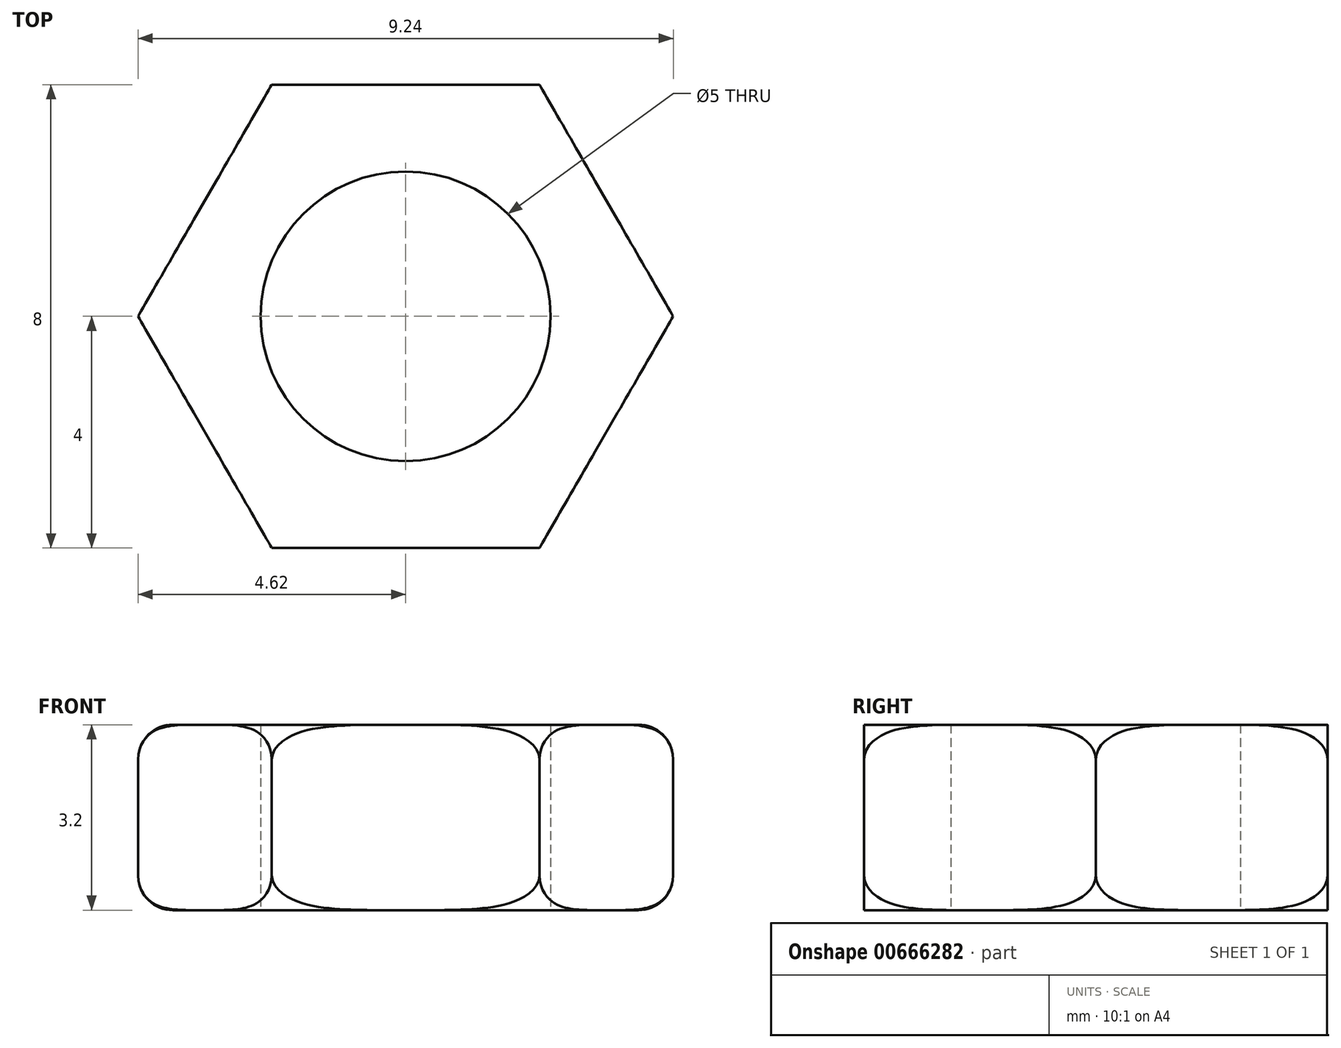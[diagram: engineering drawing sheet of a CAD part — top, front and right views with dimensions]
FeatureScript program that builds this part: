
annotation { "Feature Type Name" : "Feature", "Feature Type Description" : "" }
export const myFeature = defineFeature(function(context is Context, id is Id, definition is map)
    precondition{}
    {
        {
            var Q0;
            Q0=qCreatedBy(makeId("Top.planeOp"),FACE);
            var sketch = newSketch(context, id + "F0", { "sketchPlane" : qUnion([Q0])});
            skCircle(sketch, "E0", {"center": v(0, 0) * mm, "radius": 4.62 * mm});
            skCircle(sketch, "E1.cCircle", {"center": v(0, 0) * mm, "radius": 4 * mm, "construction": true});
            skLineSegment(sketch, "E1.0", {"start": v(-4.62, 0) * mm, "end": v(-2.3, 4) * mm, "construction": true});
            skLineSegment(sketch, "E1.1", {"start": v(-2.3, 4) * mm, "end": v(2.3, 4) * mm, "construction": true});
            skLineSegment(sketch, "E1.2", {"start": v(2.3, 4) * mm, "end": v(4.62, 0) * mm, "construction": true});
            skLineSegment(sketch, "E1.3", {"start": v(4.62, 0) * mm, "end": v(2.3, -4) * mm, "construction": true});
            skLineSegment(sketch, "E1.4", {"start": v(2.3, -4) * mm, "end": v(-2.3, -4) * mm, "construction": true});
            skLineSegment(sketch, "E1.5", {"start": v(-2.3, -4) * mm, "end": v(-4.62, 0) * mm, "construction": true});
            skPoint(sketch, "E1.0.midPoint", {"position": v(-3.46, 2) * mm});
            skCircle(sketch, "E2", {"center": v(0, 0) * mm, "radius": 2.5 * mm});
            skSolve(sketch);
        }
        {
            var Q0;
            Q0 = qSketchRegion(id + "F0", true);
            extrude(context, id + "F1", {"entities" : qUnion([Q0]), "depth" : 3.2 * mm, "offsetDistance" : 25 * mm, "symmetric" : true});
        }
        {
            var Q0;
            Q0=makeQuery(id+"F1.opExtrude","CAP_EDGE",EDGE,{"disambiguationData":[OSD([sQuery(id+"F0.wireOp",EDGE,"E0")])],"isStart":false});
            var Q1;
            Q1=makeQuery(id+"F1.opExtrude","CAP_EDGE",EDGE,{"disambiguationData":[OSD([sQuery(id+"F0.wireOp",EDGE,"E0")])],"isStart":true});
            fillet(context, id + "F2", {"entities" : qUnion([Q0, Q1]), "radius" : 0.6 * mm, "tangentPropagation" : true, "allowEdgeOverflow" : false});
        }
        {
            var Q0;
            Q0=makeQuery(id+"F1.opExtrude","CAP_FACE",FACE,{"disambiguationData":[OSD([sQuery(id+"F0.wireOp",EDGE,"E0"),sQuery(id+"F0.wireOp",EDGE,"E2")])],"isStart":false});
            var sketch = newSketch(context, id + "F3", { "sketchPlane" : qUnion([Q0])});
            skCircle(sketch, "E3.cCircle", {"center": v(0, 0) * mm, "radius": 4 * mm, "construction": true});
            skLineSegment(sketch, "E3.0", {"start": v(-4.62, 0) * mm, "end": v(-2.3, 4) * mm});
            skLineSegment(sketch, "E3.1", {"start": v(-2.3, 4) * mm, "end": v(2.3, 4) * mm});
            skLineSegment(sketch, "E3.2", {"start": v(2.3, 4) * mm, "end": v(4.62, 0) * mm});
            skLineSegment(sketch, "E3.3", {"start": v(4.62, 0) * mm, "end": v(2.3, -4) * mm});
            skLineSegment(sketch, "E3.4", {"start": v(2.3, -4) * mm, "end": v(-2.3, -4) * mm});
            skLineSegment(sketch, "E3.5", {"start": v(-2.3, -4) * mm, "end": v(-4.62, 0) * mm});
            skPoint(sketch, "E3.0.midPoint", {"position": v(-3.46, 2) * mm});
            skCircle(sketch, "E4", {"center": v(0, 0) * mm, "radius": 7.5 * mm});
            skSolve(sketch);
        }
        {
            var Q0;
            Q0 = qSketchRegion(id + "F3", true);
            extrude(context, id + "F4", {"entities" : qUnion([Q0]), "operationType" : NewBodyOperationType.REMOVE, "endBound" : BoundingType.THROUGH_ALL, "oppositeDirection" : true, "depth" : 25 * mm, "offsetDistance" : 25 * mm});
        }
    });
